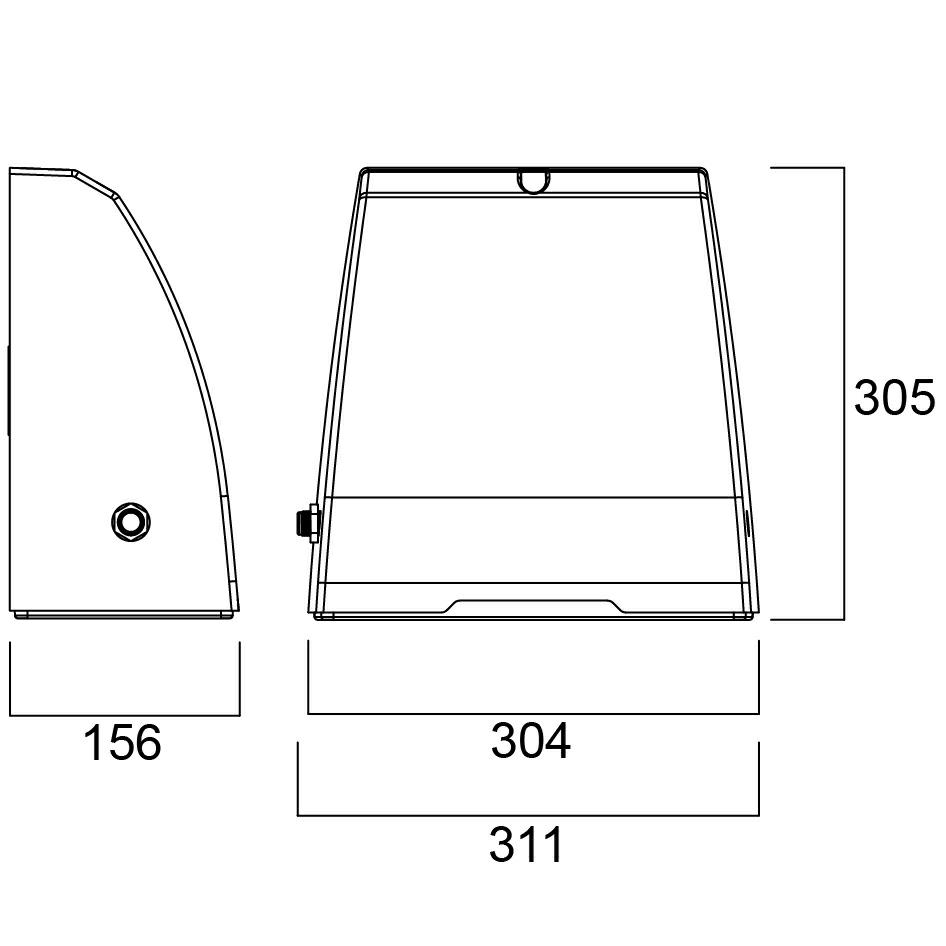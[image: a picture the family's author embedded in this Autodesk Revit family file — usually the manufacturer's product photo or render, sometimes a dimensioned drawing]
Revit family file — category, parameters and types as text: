
# Revit family: 0049945_1700lm
name_source: partatom
category: Lighting Fixtures
revit_build: Autodesk Revit 2018 (Build: 20170223_1515(x64)
units: mm (PartAtom-declared; Revit-internal decimal feet)

## family parameters
Cut with Voids When Loaded = No
Host = Face
Light Source = Yes
OmniClass Number = 23.80.70.00
OmniClass Title = Lighting
Part Type = Normal
Room Calculation Point = No
Round Connector Dimension = Use Diameter
Shared = No

## types (1)
- 0049945 MURO SURF IP65 1700-3250LM 840 PH E3 GR
    Apparent Load = 30 VA
    Assembly Code = D5020200
    AssetType = Fixed
    ClassificationName = Uniclass2015
    ClassificationValue = EF_70_80
    Color Filter = 16777215
    Cost = 0 $
    Default Elevation = 1219 mm
    Description = Muro Surface is a wall mounted fixture for exterior lighting applications with 3 hours combined non-maintained emergency unit. Comes with aluminium housing in RAL7016 anthracite grey colour, frosted PC diffuser, IP65, IK10, Class I, 4000K, non-dimmable multipower driver with 5 settings, 1700 / 1900 / 2750 / 3150 / 3250 lm, 16 / 18 / 26 / 29 / 30 W, up to 109 lm/W total system efficacy, switchable built in Mini photocell, CRI80, Asymmetrical beam, 119.000 hrs L70B50 lifespan, 304 x 305 x 155 mm (L x W x D) dimensions, 4.32 kg weight.
    Dimming Lamp Color Temperature Shift = <None>
    DocumentationLiterature = http://www.sylvania-lighting.com
    ElectricShockClassification = 108
    Emit Shape Visible in Rendering = No
    Emit from Circle Diameter = 610 mm
    IfcExportAs = Class I
    IfcExportType = IfcLightFixtureType
    ImpactProtectionIndex = IfcLightFixtureType
    IngressProtection = IfcLightFixtureType
    InputNominalFrequency = 4000
    InputVoltage = 0
    LampColourRenderingIndex = 16500
    LampColourTemperature = LED
    LampMacAdamStep = 80
    LampNominalLuminous = 4000 K
    LightOutputRatio = LED
    LuminaireType = 0
    ManufacturerName = 108 lm/W
    Material = Feilo Sylvania
    Material_1_SYL = <By Category>
    Material_2_SYL = <By Category>
    Material_3_SYL = <By Category>
    Material_4_SYL = <By Category>
    Model = Muro Surface IP65 1700-3250lm 840 PH E3 Grey
    ModelNumber = 0049945
    ModelReference = Muro Surface IP65 1700-3250lm 840 PH E3 Grey
    Name = Muro Surface IP65 1700-3250lm 840 PH E3 Grey
    NominalDepth = 155 mm  [stored 0.50853 ft]
    NominalHeight = 305 mm  [stored 1.00066 ft]
    NominalLength = 155 mm  [stored 0.50853 ft]
    Photometric Web File = 0049945_1700lm.IES
    PowerConsumption = Lighting
    PowerFactor = 0.95
    Tilt Angle = -90.00°
    Type Image = <None>
    TypeName = Muro Surface IP65 1700-3250lm 840 PH E3 Grey
    URL = 0.9
    Voltage = 0 V
    WarrantyDescription = http://www.sylvania-lighting.com

note: [stored X ft] marks values corroborated as IEEE doubles in the binary element streams (Revit-internal decimal feet)

## geometry (parser evidence)
native form markers: Sweep x1
no freeform markers — native parametric forms only
